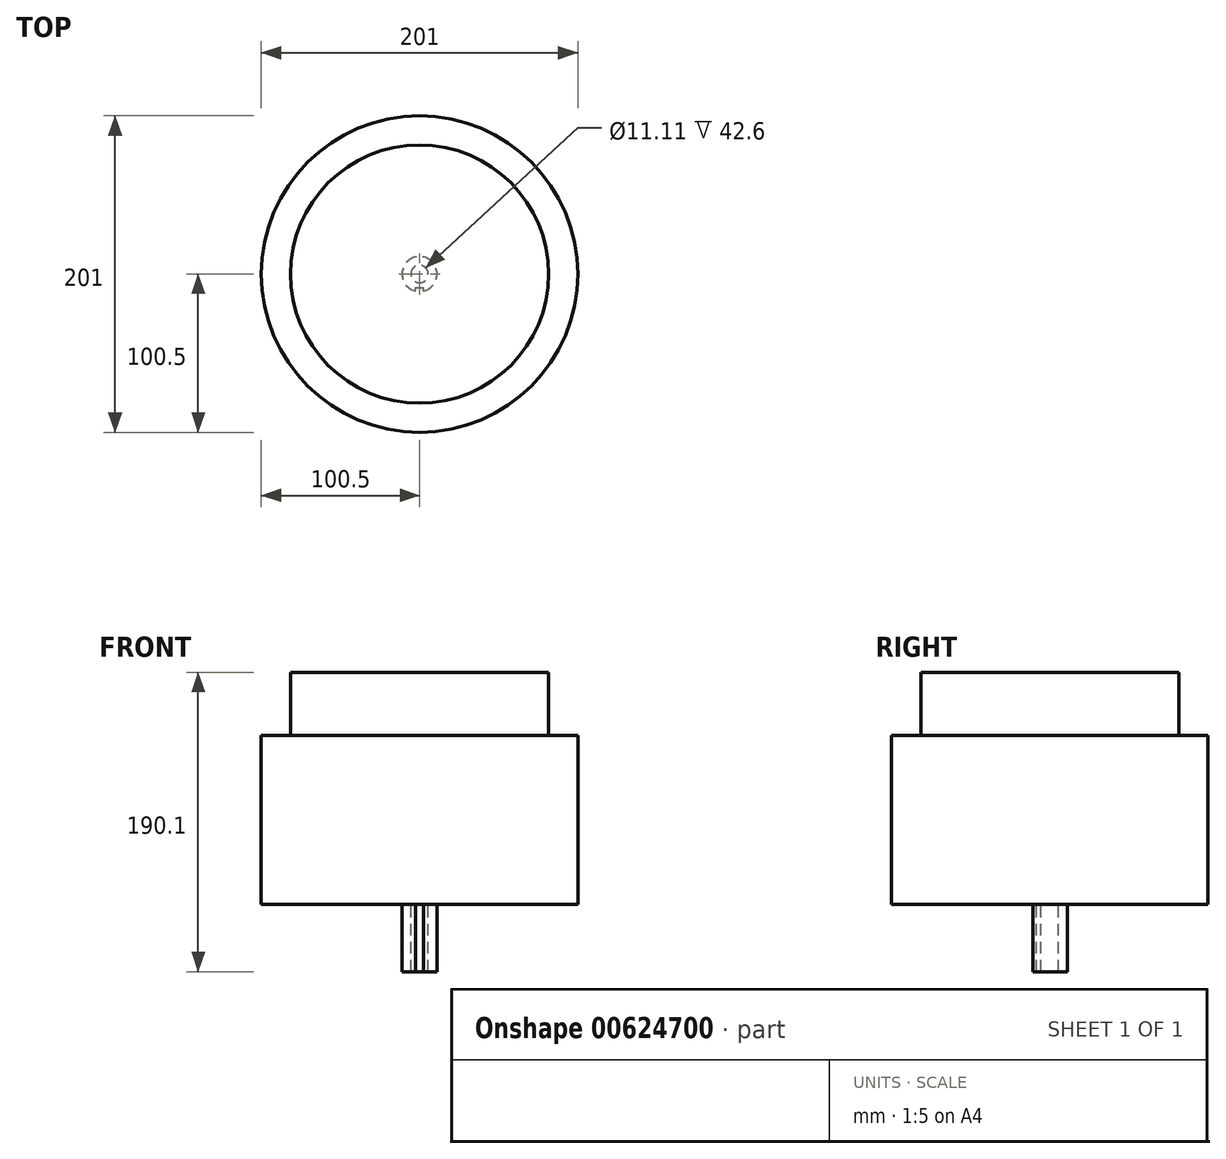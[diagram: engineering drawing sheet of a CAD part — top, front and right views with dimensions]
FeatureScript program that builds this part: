
annotation { "Feature Type Name" : "Feature", "Feature Type Description" : "" }
export const myFeature = defineFeature(function(context is Context, id is Id, definition is map)
    precondition{}
    {
        {
            var Q0;
            Q0=qCreatedBy(makeId("Top.planeOp"),FACE);
            var sketch = newSketch(context, id + "F0", { "sketchPlane" : qUnion([Q0])});
            skCircle(sketch, "E0", {"center": v(0, 0) * mm, "radius": 100.5 * mm});
            skSolve(sketch);
        }
        {
            var Q0;
            Q0=makeQuery(id+"F0.imprint","IMPRINT",FACE,{"disambiguationData":[TD([[makeQuery(id+"F0.imprint","IMPRINT",EDGE,{"derivedFrom":sQuery(id+"F0.wireOp",EDGE,"E0")}),1.0]])]});
            extrude(context, id + "F1", {"entities" : qUnion([Q0]), "depth" : 107.5 * mm, "offsetDistance" : 25 * mm});
        }
        {
            var Q0;
            Q0=makeQuery(id+"F1.opExtrude","CAP_FACE",FACE,{"disambiguationData":[OSD([sQuery(id+"F0.wireOp",EDGE,"E0")])],"isStart":false});
            var sketch = newSketch(context, id + "F2", { "sketchPlane" : qUnion([Q0])});
            skCircle(sketch, "E1", {"center": v(0, 0) * mm, "radius": 82 * mm});
            skSolve(sketch);
        }
        {
            var Q0;
            Q0=makeQuery(id+"F2.imprint","IMPRINT",FACE,{"disambiguationData":[TD([[makeQuery(id+"F2.imprint","IMPRINT",EDGE,{"derivedFrom":sQuery(id+"F2.wireOp",EDGE,"E1")}),1.0]])]});
            extrude(context, id + "F3", {"entities" : qUnion([Q0]), "operationType" : NewBodyOperationType.ADD, "depth" : 40 * mm, "offsetDistance" : 25 * mm});
        }
        {
            var Q0;
            Q0=makeQuery(id+"F1.opExtrude","CAP_FACE",FACE,{"disambiguationData":[OSD([sQuery(id+"F0.wireOp",EDGE,"E0")])],"isStart":true});
            var sketch = newSketch(context, id + "F4", { "sketchPlane" : qUnion([Q0])});
            skCircle(sketch, "E2", {"center": v(0, 0) * mm, "radius": 11.1 * mm});
            skLineSegment(sketch, "E3", {"start": v(0, 0) * mm, "end": v(0, 11.1) * mm});
            skLineSegment(sketch, "E4.bottom", {"start": v(-2.4, 13.76) * mm, "end": v(2.4, 13.76) * mm});
            skLineSegment(sketch, "E4.top", {"start": v(-2.4, 8.46) * mm, "end": v(2.4, 8.46) * mm});
            skLineSegment(sketch, "E4.left", {"start": v(-2.4, 13.76) * mm, "end": v(-2.4, 8.46) * mm});
            skLineSegment(sketch, "E4.right", {"start": v(2.4, 13.76) * mm, "end": v(2.4, 8.46) * mm});
            skPoint(sketch, "E4.middle", {"position": v(0, 11.1) * mm});
            skCircle(sketch, "E5", {"center": v(0, 0) * mm, "radius": 5.55 * mm});
            skSolve(sketch);
        }
        {
            var Q0;
            Q0=makeQuery(id+"F4.imprint","IMPRINT",FACE,{"disambiguationData":[TD([[makeQuery(id+"F4.imprint","IMPRINT",EDGE,{"derivedFrom":sQuery(id+"F4.wireOp",EDGE,"E5")}),-1.0]])]});
            extrude(context, id + "F5", {"entities" : qUnion([Q0]), "operationType" : NewBodyOperationType.ADD, "depth" : 42.6 * mm, "offsetDistance" : 25 * mm});
        }
    });
